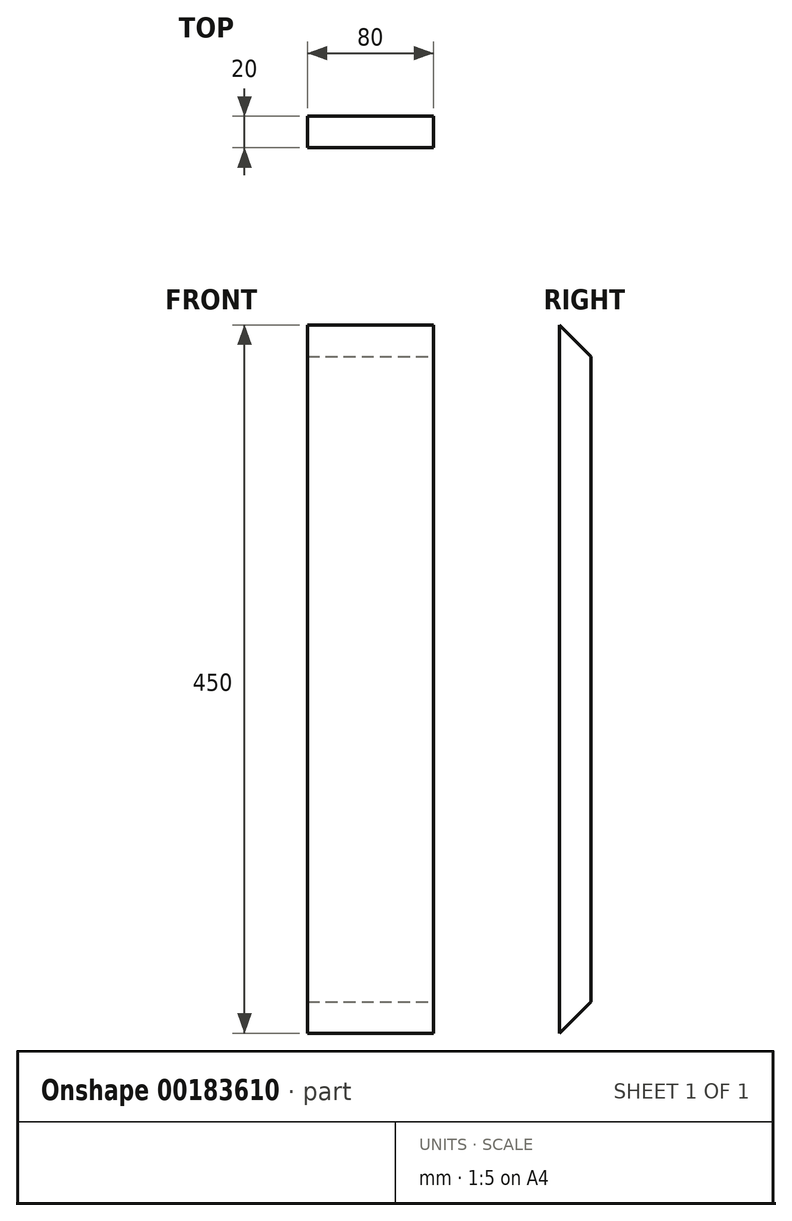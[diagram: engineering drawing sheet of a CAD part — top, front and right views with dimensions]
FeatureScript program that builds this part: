
annotation { "Feature Type Name" : "Feature", "Feature Type Description" : "" }
export const myFeature = defineFeature(function(context is Context, id is Id, definition is map)
    precondition{}
    {
        {
            var Q0;
            Q0=qCreatedBy(makeId("Front.planeOp"),FACE);
            var sketch = newSketch(context, id + "F0", { "sketchPlane" : qUnion([Q0])});
            skLineSegment(sketch, "E0.bottom", {"start": v(40, 225) * mm, "end": v(-40, 225) * mm});
            skLineSegment(sketch, "E0.top", {"start": v(40, -225) * mm, "end": v(-40, -225) * mm});
            skLineSegment(sketch, "E0.left", {"start": v(40, 225) * mm, "end": v(40, -225) * mm});
            skLineSegment(sketch, "E0.right", {"start": v(-40, 225) * mm, "end": v(-40, -225) * mm});
            skPoint(sketch, "E0.middle", {"position": v(0, 0) * mm});
            skSolve(sketch);
        }
        {
            var Q0;
            Q0 = qSketchRegion(id + "F0", true);
            extrude(context, id + "F1", {"entities" : qUnion([Q0]), "depth" : 20 * mm});
        }
        {
            var Q0;
            Q0=makeQuery(id+"F1.opExtrude","SWEPT_FACE",FACE,{"disambiguationData":[OSD([sQuery(id+"F0.wireOp",EDGE,"E0.left")])]});
            var sketch = newSketch(context, id + "F2", { "sketchPlane" : qUnion([Q0])});
            skLineSegment(sketch, "E1", {"start": v(-20, 225) * mm, "end": v(0, 225) * mm});
            skLineSegment(sketch, "E2", {"start": v(0, 225) * mm, "end": v(0, 205) * mm});
            skLineSegment(sketch, "E3", {"start": v(0, 205) * mm, "end": v(-20, 225) * mm});
            skLineSegment(sketch, "E4", {"start": v(-20, -225) * mm, "end": v(0, -205) * mm});
            skLineSegment(sketch, "E5", {"start": v(0, -205) * mm, "end": v(0, -225) * mm});
            skLineSegment(sketch, "E6", {"start": v(0, -225) * mm, "end": v(-20, -225) * mm});
            skSolve(sketch);
        }
        {
            var Q0;
            Q0 = qSketchRegion(id + "F2", true);
            extrude(context, id + "F3", {"entities" : qUnion([Q0]), "operationType" : NewBodyOperationType.REMOVE, "oppositeDirection" : true, "depth" : 80 * mm});
        }
    });
